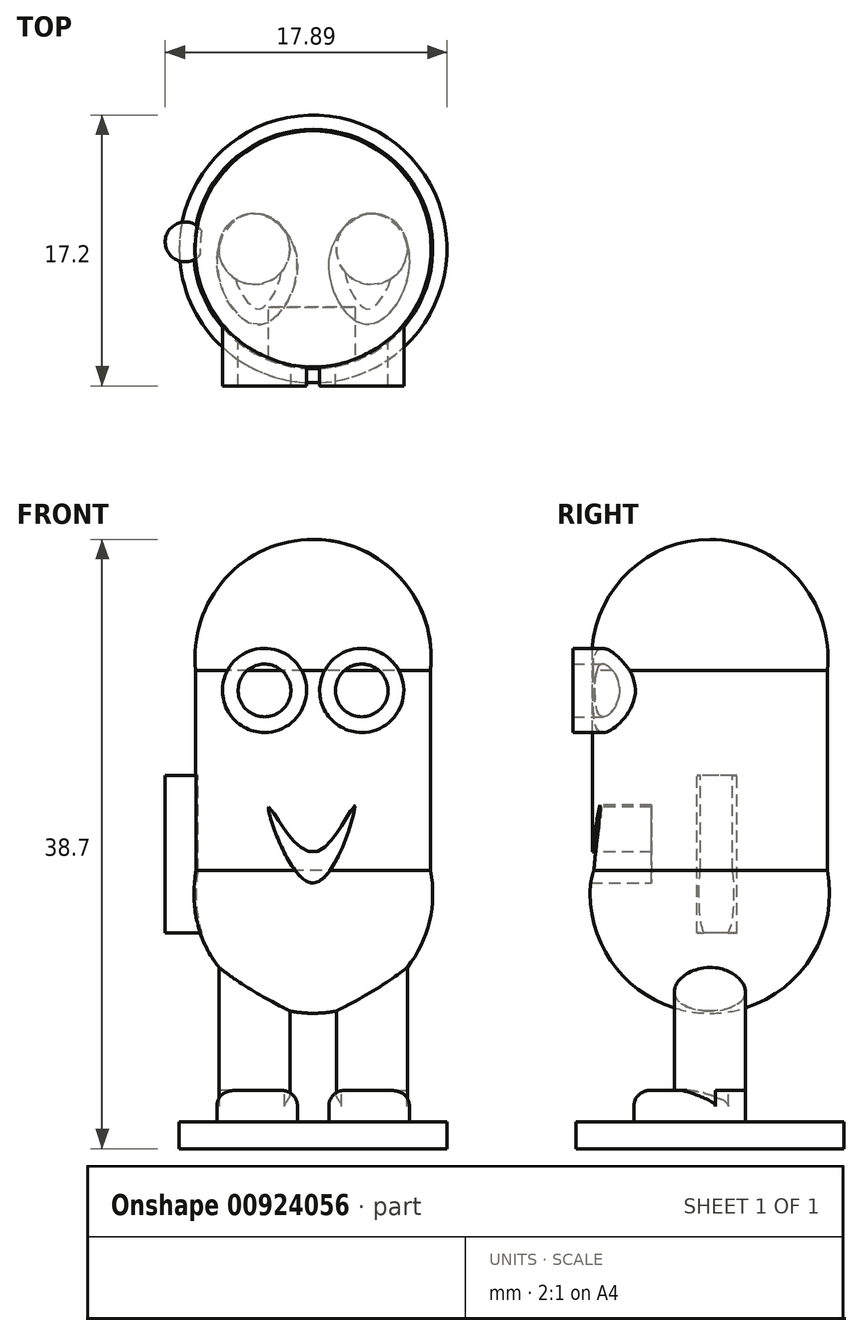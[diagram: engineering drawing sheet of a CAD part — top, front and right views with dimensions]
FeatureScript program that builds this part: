
annotation { "Feature Type Name" : "Feature", "Feature Type Description" : "" }
export const myFeature = defineFeature(function(context is Context, id is Id, definition is map)
    precondition{}
    {
        {
            var Q0;
            Q0=qCreatedBy(makeId("Front.planeOp"),FACE);
            var sketch = newSketch(context, id + "F0", { "sketchPlane" : qUnion([Q0])});
            skLineSegment(sketch, "E0.left", {"start": v(-7.46, 7.5) * mm, "end": v(-7.46, -7.5) * mm});
            skPoint(sketch, "E0.middle", {"position": v(0, 0) * mm});
            skArc(sketch, "E1", {"start": v(0, 15) * mm, "mid": v(-5.58, 12.5) * mm, "end": v(-7.46, 6.69) * mm});
            skLineSegment(sketch, "E2", {"start": v(0, 15) * mm, "end": v(0, -15.1) * mm});
            skPoint(sketch, "E3.orphan", {"position": v(7.46, 7.5) * mm});
            skPoint(sketch, "E0.right.end.orphan", {"position": v(7.46, -7.5) * mm});
            skArc(sketch, "E4.trimOffspring", {"start": v(-7.46, -6.03) * mm, "mid": v(-5.87, -12.33) * mm, "end": v(0, -15.1) * mm});
            skSolve(sketch);
        }
        {
            var Q0;
            {var subQ0=sQuery(id+"F0.wireOp",EDGE,"E1");Q0=makeQuery(id+"F0.imprint","IMPRINT",FACE,{"disambiguationData":[TD([[makeQuery(id+"F0.imprint","IMPRINT",EDGE,{"derivedFrom":subQ0}),1.0]])]});}
            var Q1;
            Q1=sQuery(id+"F0.wireOp",EDGE,"E2");
            revolve(context, id + "F1", {"surfaceOperationType" : NewSurfaceOperationType.NEW, "entities" : qUnion([Q0]), "axis" : qUnion([Q1]), "revolveType" : RevolveType.FULL});
        }
        {
            var Q0;
            Q0=qCreatedBy(makeId("Front.planeOp"),FACE);
            var sketch = newSketch(context, id + "F2", { "sketchPlane" : qUnion([Q0])});
            skLineSegment(sketch, "E5", {"start": v(0, 9.64) * mm, "end": v(0, -4.34) * mm});
            skCircle(sketch, "E6", {"center": v(-3.09, 5.4) * mm, "radius": 2.67 * mm});
            skCircle(sketch, "E7", {"center": v(-3.09, 5.4) * mm, "radius": 1.67 * mm});
            skCircle(sketch, "E8.MirrorC", {"center": v(3.09, 5.4) * mm, "radius": 1.67 * mm});
            skCircle(sketch, "E9.MirrorC", {"center": v(3.09, 5.4) * mm, "radius": 2.67 * mm});
            skSolve(sketch);
        }
        {
            var Q0;
            Q0 = qSketchRegion(id + "F2", true);
            extrude(context, id + "F3", {"entities" : qUnion([Q0]), "operationType" : NewBodyOperationType.ADD, "depth" : 8.7 * mm, "offsetDistance" : 25 * mm});
        }
        {
            var Q0;
            Q0=makeQuery(id+"F3.opExtrude","CAP_FACE",FACE,{"disambiguationData":[OSD([sQuery(id+"F2.wireOp",EDGE,"E6"),sQuery(id+"F2.wireOp",EDGE,"E7")])],"isStart":false});
            var sketch = newSketch(context, id + "F4", { "sketchPlane" : qUnion([Q0])});
            skFitSpline(sketch, "E10", {"points": [v(-2.83, -2) * mm, v(0, -6.83) * mm, v(2.64, -1.86) * mm, v(0, -4.86) * mm, v(-2.83, -2) * mm]});
            skSolve(sketch);
        }
        {
            var Q0;
            Q0=makeQuery(id+"F4.imprint","IMPRINT",FACE,{"disambiguationData":[TD([[makeQuery(id+"F4.imprint","IMPRINT",EDGE,{"derivedFrom":sQuery(id+"F4.wireOp",EDGE,"E10")}),1.0]])]});
            extrude(context, id + "F5", {"entities" : qUnion([Q0]), "operationType" : NewBodyOperationType.REMOVE, "oppositeDirection" : true, "depth" : 5 * mm, "offsetDistance" : 25 * mm});
        }
        {
            var Q0;
            Q0=qCreatedBy(makeId("Top.planeOp"),FACE);
            var sketch = newSketch(context, id + "F6", { "sketchPlane" : qUnion([Q0])});
            skCircle(sketch, "E11", {"center": v(-8.13, 0.45) * mm, "radius": 1.26 * mm});
            skLineSegment(sketch, "E12", {"start": v(0, 5.13) * mm, "end": v(0, -4.69) * mm});
            skCircle(sketch, "E13.MirrorC", {"center": v(8.13, 0.45) * mm, "radius": 1.26 * mm});
            skSolve(sketch);
        }
        {
            var Q0;
            Q0=makeQuery(id+"F6.imprint","IMPRINT",FACE,{"disambiguationData":[TD([[makeQuery(id+"F6.imprint","IMPRINT",EDGE,{"derivedFrom":sQuery(id+"F6.wireOp",EDGE,"E11")}),1.0]])]});
            var Q1;
            Q1=makeQuery(id+"F6.imprint","IMPRINT",FACE,{"disambiguationData":[TD([[makeQuery(id+"F6.imprint","IMPRINT",EDGE,{"derivedFrom":sQuery(id+"F6.wireOp",EDGE,"E13.MirrorC")}),-1.0]])]});
            extrude(context, id + "F7", {"entities" : qUnion([Q0, Q1]), "operationType" : NewBodyOperationType.ADD, "oppositeDirection" : true, "depth" : 10 * mm, "offsetDistance" : 25 * mm});
        }
        {
            var Q0;
            Q0=qCreatedBy(makeId("Top.planeOp"),FACE);
            var sketch = newSketch(context, id + "F8", { "sketchPlane" : qUnion([Q0])});
            skLineSegment(sketch, "E14", {"start": v(0, 5.05) * mm, "end": v(0, -5.45) * mm});
            skCircle(sketch, "E15", {"center": v(-3.73, 0) * mm, "radius": 2.25 * mm});
            skCircle(sketch, "E16.MirrorC", {"center": v(3.73, 0) * mm, "radius": 2.25 * mm});
            skSolve(sketch);
        }
        {
            var Q0;
            Q0 = qSketchRegion(id + "F8", true);
            extrude(context, id + "F9", {"entities" : qUnion([Q0]), "operationType" : NewBodyOperationType.ADD, "oppositeDirection" : true, "depth" : 20 * mm, "offsetDistance" : 25 * mm});
        }
        {
            var Q0;
            Q0=makeQuery(id+"F9.opExtrude","CAP_FACE",FACE,{"disambiguationData":[OSD([sQuery(id+"F8.wireOp",EDGE,"E15")])],"isStart":false});
            var sketch = newSketch(context, id + "F10", { "sketchPlane" : qUnion([Q0])});
            skLineSegment(sketch, "E17", {"start": v(0, 5.78) * mm, "end": v(0, -6.1) * mm});
            skFitSpline(sketch, "E18", {"points": [v(-3.96, -2.24) * mm, v(-5.96, -0.35) * mm, v(-5.24, 3.61) * mm, v(-3.07, 4.77) * mm, v(-1.05, 1.77) * mm, v(-1.82, -1.2) * mm, v(-3.96, -2.24) * mm]});
            skFitSpline(sketch, "E19.MirrorC", {"points": [v(3.96, -2.24) * mm, v(5.96, -0.35) * mm, v(5.24, 3.61) * mm, v(3.07, 4.77) * mm, v(1.05, 1.77) * mm, v(1.82, -1.2) * mm, v(3.96, -2.24) * mm]});
            skSolve(sketch);
        }
        {
            var Q0;
            Q0 = qSketchRegion(id + "F10", true);
            extrude(context, id + "F11", {"entities" : qUnion([Q0]), "operationType" : NewBodyOperationType.ADD, "depth" : 2 * mm, "offsetDistance" : 25 * mm});
        }
        {
            var Q0;
            {var subQ0=sQuery(id+"F10.wireOp",EDGE,"E18");Q0=makeQuery(id+"F11.boolean.opBoolean","SPLIT",EDGE,{"disambiguationData":[topologyDisambiguationEdgeConnected([makeQuery(id+"F11.opExtrude","SWEPT_FACE",FACE,{"disambiguationData":[OSD([subQ0])]}),makeQuery(id+"F11.opExtrude","CAP_FACE",FACE,{"disambiguationData":[OSD([subQ0])],"isStart":true})])],"derivedFrom":makeQuery(id+"F11.opExtrude","CAP_EDGE",EDGE,{"disambiguationData":[OSD([subQ0])],"isStart":true})});}
            var Q1;
            {var subQ0=sQuery(id+"F10.wireOp",EDGE,"E19.MirrorC");Q1=makeQuery(id+"F11.boolean.opBoolean","SPLIT",EDGE,{"disambiguationData":[topologyDisambiguationEdgeConnected([makeQuery(id+"F11.opExtrude","SWEPT_FACE",FACE,{"disambiguationData":[OSD([subQ0])]}),makeQuery(id+"F11.opExtrude","CAP_FACE",FACE,{"disambiguationData":[OSD([subQ0])],"isStart":true})])],"derivedFrom":makeQuery(id+"F11.opExtrude","CAP_EDGE",EDGE,{"disambiguationData":[OSD([subQ0])],"isStart":true})});}
            fillet(context, id + "F12", {"entities" : qUnion([Q0, Q1]), "radius" : 1 * mm, "tangentPropagation" : true, "allowEdgeOverflow" : false});
        }
        {
            var Q0;
            Q0=makeQuery(id+"F11.opExtrude","CAP_FACE",FACE,{"disambiguationData":[OSD([sQuery(id+"F10.wireOp",EDGE,"E18")])],"isStart":false});
            var sketch = newSketch(context, id + "F13", { "sketchPlane" : qUnion([Q0])});
            skCircle(sketch, "E20", {"center": v(0, 0) * mm, "radius": 8.5 * mm});
            skSolve(sketch);
        }
        {
            var Q0;
            Q0=makeQuery(id+"F13.imprint","IMPRINT",FACE,{"disambiguationData":[TD([[makeQuery(id+"F13.imprint","IMPRINT",EDGE,{"derivedFrom":sQuery(id+"F13.wireOp",EDGE,"E20")}),1.0]])]});
            var Q1;
            Q1=makeQuery(id+"F13.imprint","IMPRINT",FACE,{"disambiguationData":[TD([[makeQuery(id+"F13.imprint","IMPRINT",EDGE,{"derivedFrom":makeQuery(id+"F11.opExtrude","CAP_EDGE",EDGE,{"disambiguationData":[OSD([sQuery(id+"F10.wireOp",EDGE,"E18")])],"isStart":false})}),-1.0]])]});
            extrude(context, id + "F14", {"entities" : qUnion([Q0, Q1]), "operationType" : NewBodyOperationType.ADD, "depth" : 1.7 * mm, "offsetDistance" : 25 * mm});
        }
    });
